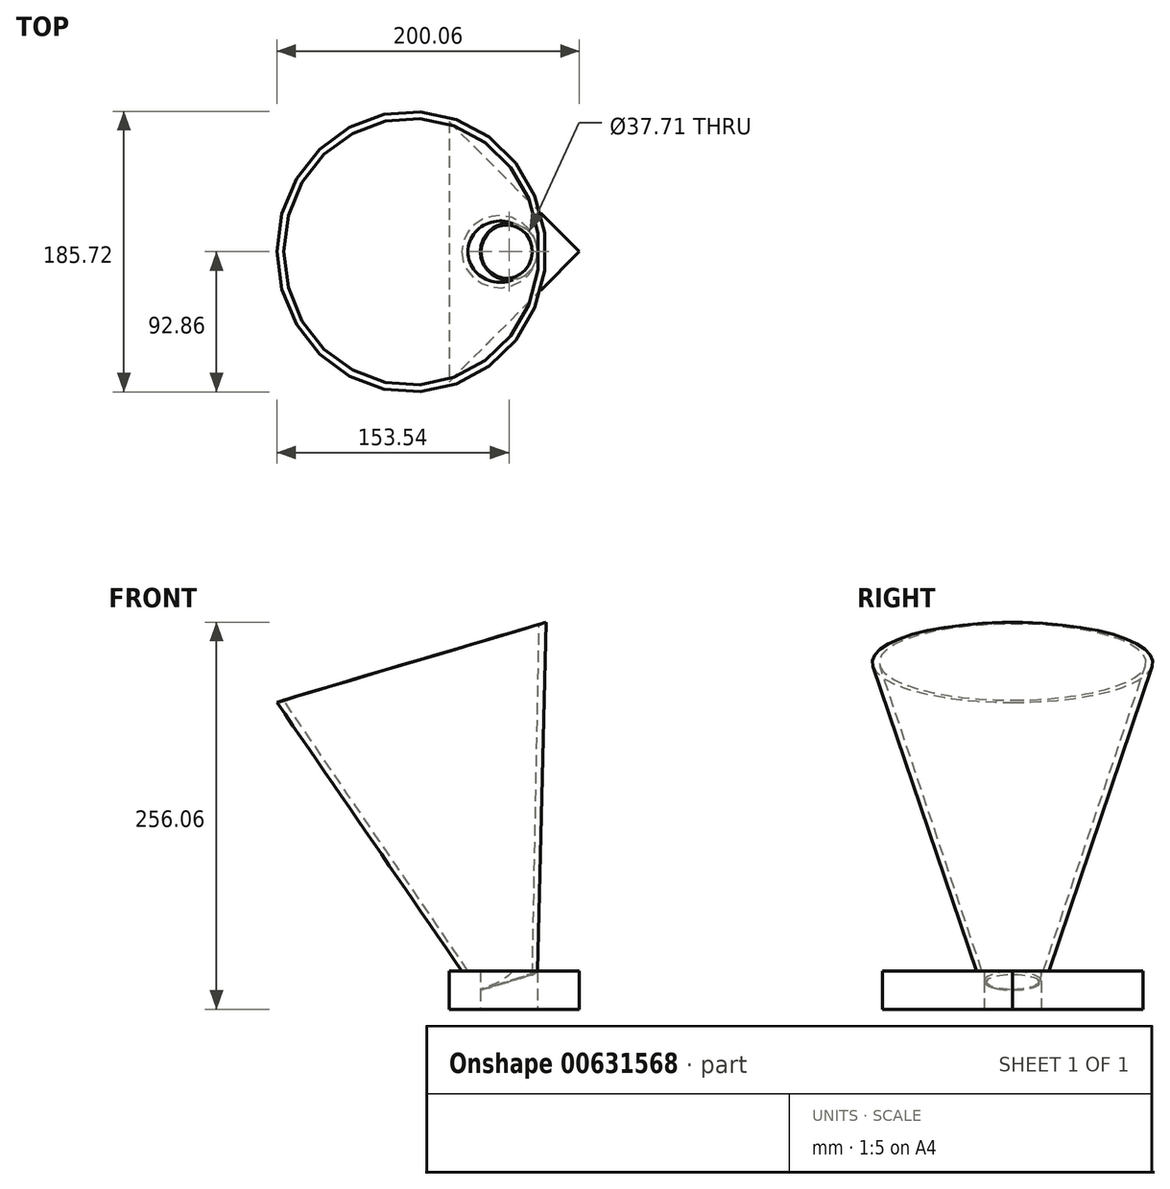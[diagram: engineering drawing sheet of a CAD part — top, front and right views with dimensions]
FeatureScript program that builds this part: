
annotation { "Feature Type Name" : "Feature", "Feature Type Description" : "" }
export const myFeature = defineFeature(function(context is Context, id is Id, definition is map)
    precondition{}
    {
        {
            var Q0;
            Q0=qCreatedBy(makeId("Front.planeOp"),FACE);
            var sketch = newSketch(context, id + "F0", { "sketchPlane" : qUnion([Q0])});
            skLineSegment(sketch, "E0.bottom", {"start": v(-45.08, 0) * mm, "end": v(45.08, 0) * mm});
            skLineSegment(sketch, "E0.top", {"start": v(-45.08, 0) * mm, "end": v(-22.54, 0) * mm});
            skLineSegment(sketch, "E0.left", {"start": v(-45.08, 0) * mm, "end": v(-45.08, 0) * mm});
            skLineSegment(sketch, "E0.right", {"start": v(45.08, 0) * mm, "end": v(45.08, 0) * mm});
            skPoint(sketch, "E0.middle", {"position": v(0, 0) * mm});
            skLineSegment(sketch, "E1", {"start": v(0, 0) * mm, "end": v(22.54, 0) * mm});
            skLineSegment(sketch, "E2", {"start": v(22.54, 0) * mm, "end": v(45.08, 0) * mm});
            skLineSegment(sketch, "E3", {"start": v(-22.54, 0) * mm, "end": v(-18.45, 0) * mm});
            skLineSegment(sketch, "E4.bottom", {"start": v(-45.08, 0) * mm, "end": v(45.09, 0) * mm});
            skLineSegment(sketch, "E4.top", {"start": v(-45.08, 18.84) * mm, "end": v(45.09, 18.84) * mm});
            skLineSegment(sketch, "E4.left", {"start": v(-45.08, 0) * mm, "end": v(-45.08, 18.84) * mm});
            skLineSegment(sketch, "E4.right", {"start": v(45.09, 0) * mm, "end": v(45.09, 18.84) * mm});
            skLineSegment(sketch, "E5", {"start": v(22.54, 0) * mm, "end": v(22.54, 249.84) * mm});
            skLineSegment(sketch, "E6", {"start": v(-22.54, 0) * mm, "end": v(-153.54, 190.4) * mm});
            skLineSegment(sketch, "E7", {"start": v(22.54, 249.84) * mm, "end": v(22.54, 249.84) * mm});
            skLineSegment(sketch, "E8", {"start": v(-153.54, 190.4) * mm, "end": v(-153.54, 190.4) * mm});
            skLineSegment(sketch, "E9", {"start": v(22.54, 249.84) * mm, "end": v(-65.5, 220.12) * mm});
            skLineSegment(sketch, "E10", {"start": v(-65.5, 220.12) * mm, "end": v(-149.18, 191.86) * mm});
            skLineSegment(sketch, "E11", {"start": v(0, 0) * mm, "end": v(-65.5, 220.12) * mm});
            skLineSegment(sketch, "E12", {"start": v(-18.45, 0) * mm, "end": v(0, 0) * mm});
            skLineSegment(sketch, "E13", {"start": v(-149.18, 191.86) * mm, "end": v(-153.54, 190.4) * mm});
            skLineSegment(sketch, "E14", {"start": v(-149.18, 191.86) * mm, "end": v(-18.45, 0) * mm});
            skFitSpline(sketch, "E15", {"points": [v(22.54, 42.39) * mm, v(45.09, 18.84) * mm], "startDerivative": vector(12.44, -42.2) * mm, "endDerivative": vector(45.07, -15.03) * mm});
            skSolve(sketch);
        }
        {
            var Q0;
            {var subQ5=sQuery(id+"F0.wireOp",EDGE,"E13");Q0=makeQuery(id+"F0.imprint","IMPRINT",FACE,{"disambiguationData":[TD([[makeQuery(id+"F0.imprint","IMPRINT",EDGE,{"derivedFrom":subQ5}),1.0]])]});}
            var Q1;
            {var subQ0=sQuery(id+"F0.wireOp",EDGE,"E6");var subQ5=sQuery(id+"F0.wireOp",EDGE,"E4.top");var subQ6=makeQuery(id+"F0.imprint","INTERSECT",VERTEX,{"derivedFrom":[subQ5,subQ0]});Q1=makeQuery(id+"F0.imprint","IMPRINT",FACE,{"disambiguationData":[TD([[makeQuery(id+"F0.imprint","IMPRINT",EDGE,{"disambiguationData":[TD([[subQ6,-1.0]])],"derivedFrom":subQ5}),-1.0]])]});}
            var Q2;
            Q2=sQuery(id+"F0.wireOp",EDGE,"E11");
            revolve(context, id + "F1", {"entities" : qUnion([Q0, Q1]), "axis" : qUnion([Q2]), "revolveType" : RevolveType.FULL});
        }
        {
            var Q0;
            Q0=qCreatedBy(makeId("Top.planeOp"),FACE);
            var sketch = newSketch(context, id + "F2", { "sketchPlane" : qUnion([Q0])});
            skLineSegment(sketch, "E16", {"start": v(46.52, 0) * mm, "end": v(-39.65, 0) * mm});
            skLineSegment(sketch, "E17", {"start": v(-39.65, 0) * mm, "end": v(-39.65, -86.17) * mm});
            skLineSegment(sketch, "E18", {"start": v(-39.65, -86.17) * mm, "end": v(46.52, 0) * mm});
            skLineSegment(sketch, "E19.MirrorCS", {"start": v(-39.65, 86.17) * mm, "end": v(46.52, 0) * mm});
            skLineSegment(sketch, "E20.MirrorCS", {"start": v(-39.65, 0) * mm, "end": v(-39.65, 86.17) * mm});
            skCircle(sketch, "E21", {"center": v(0, 0) * mm, "radius": 18.86 * mm});
            skSolve(sketch);
        }
        {
            var Q0;
            {var subQ1=sQuery(id+"F2.wireOp",EDGE,"E17");Q0=makeQuery(id+"F2.imprint","IMPRINT",FACE,{"disambiguationData":[TD([[makeQuery(id+"F2.imprint","IMPRINT",EDGE,{"derivedFrom":subQ1}),1.0]])]});}
            var Q1;
            {var subQ4=sQuery(id+"F2.wireOp",EDGE,"E19.MirrorCS");Q1=makeQuery(id+"F2.imprint","IMPRINT",FACE,{"disambiguationData":[TD([[makeQuery(id+"F2.imprint","IMPRINT",EDGE,{"derivedFrom":subQ4}),-1.0]])]});}
            extrude(context, id + "F3", {"entities" : qUnion([Q0, Q1]), "operationType" : NewBodyOperationType.ADD, "endBound" : BoundingType.SYMMETRIC, "depth" : 25.4 * mm, "offsetDistance" : 25.4 * mm});
        }
    });
